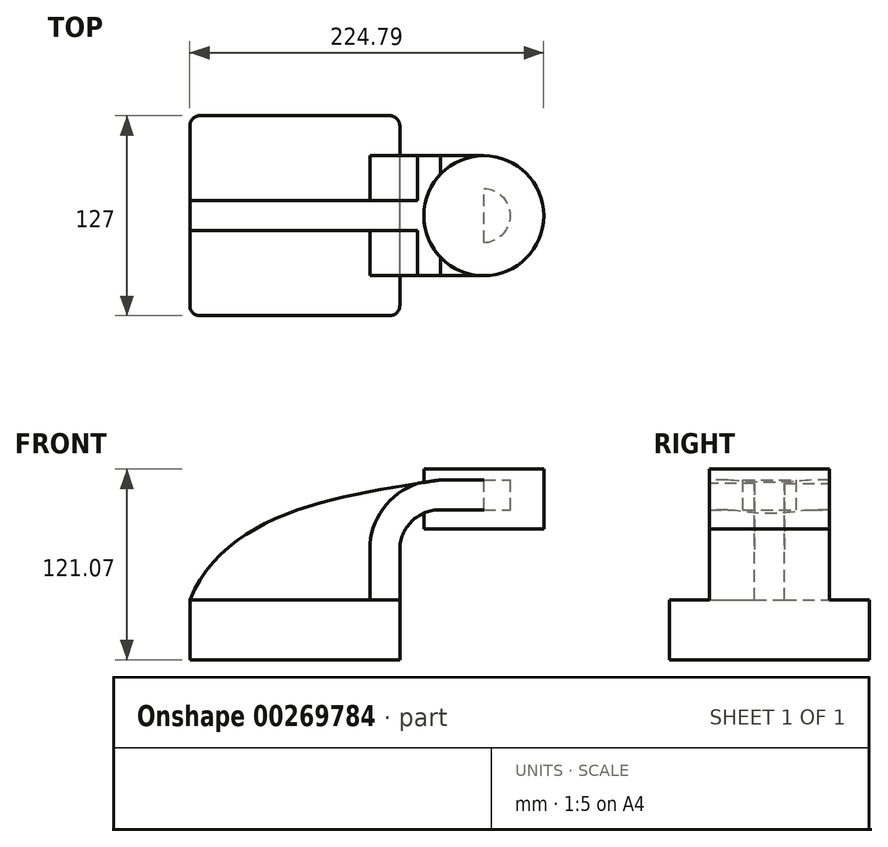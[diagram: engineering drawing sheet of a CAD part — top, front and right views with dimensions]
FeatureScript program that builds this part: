
annotation { "Feature Type Name" : "Feature", "Feature Type Description" : "" }
export const myFeature = defineFeature(function(context is Context, id is Id, definition is map)
    precondition{}
    {
        {
            var Q0;
            Q0=qCreatedBy(makeId("Front.planeOp"),FACE);
            var sketch = newSketch(context, id + "F0", { "sketchPlane" : qUnion([Q0])});
            skLineSegment(sketch, "E0.bottom", {"start": v(-66.68, 19.05) * mm, "end": v(66.67, 19.05) * mm});
            skLineSegment(sketch, "E0.top", {"start": v(-66.68, -19.05) * mm, "end": v(66.68, -19.05) * mm});
            skLineSegment(sketch, "E0.left", {"start": v(-66.68, 19.05) * mm, "end": v(-66.67, -19.05) * mm});
            skLineSegment(sketch, "E0.right", {"start": v(66.68, 19.05) * mm, "end": v(66.68, -19.05) * mm});
            skPoint(sketch, "E0.middle", {"position": v(0, 0) * mm});
            skLineSegment(sketch, "E1.bottom", {"start": v(120.01, 102.02) * mm, "end": v(158.11, 102.02) * mm});
            skLineSegment(sketch, "E1.top", {"start": v(120.01, 63.92) * mm, "end": v(158.11, 63.92) * mm});
            skLineSegment(sketch, "E1.left", {"start": v(120.01, 102.02) * mm, "end": v(120.01, 63.92) * mm});
            skLineSegment(sketch, "E1.right", {"start": v(158.11, 102.02) * mm, "end": v(158.11, 63.92) * mm});
            skPoint(sketch, "E1.middle", {"position": v(139.06, 82.97) * mm});
            skLineSegment(sketch, "E2", {"start": v(66.67, 19.05) * mm, "end": v(66.67, 50.8) * mm});
            skArc(sketch, "E3", {"start": v(66.67, 50.8) * mm, "mid": v(74.27, 68.91) * mm, "end": v(92.51, 76.2) * mm});
            skLineSegment(sketch, "E4", {"start": v(92.51, 76.2) * mm, "end": v(136.96, 76.2) * mm});
            skLineSegment(sketch, "E5.0", {"start": v(92.65, 95.25) * mm, "end": v(136.96, 95.25) * mm});
            skArc(sketch, "E5.1", {"start": v(47.62, 50.8) * mm, "mid": v(60.85, 82.43) * mm, "end": v(92.65, 95.25) * mm});
            skLineSegment(sketch, "E5.2", {"start": v(47.62, 19.05) * mm, "end": v(47.62, 50.8) * mm});
            skLineSegment(sketch, "E6", {"start": v(136.96, 95.25) * mm, "end": v(136.96, 76.2) * mm});
            skFitSpline(sketch, "E7", {"points": [v(-66.68, 19.05) * mm, v(92.65, 95.25) * mm], "startDerivative": vector(70, 169.2) * mm, "endDerivative": vector(193.9, 30.04) * mm});
            skSolve(sketch);
        }
        {
            var Q0;
            Q0=makeQuery(id+"F0.imprint","IMPRINT",FACE,{"disambiguationData":[TD([[makeQuery(id+"F0.imprint","IMPRINT",EDGE,{"derivedFrom":sQuery(id+"F0.wireOp",EDGE,"E0.top")}),1.0]])]});
            extrude(context, id + "F1", {"entities" : qUnion([Q0]), "endBound" : BoundingType.SYMMETRIC, "depth" : 127 * mm});
        }
        {
            var Q0;
            {var subQ3=sQuery(id+"F0.wireOp",EDGE,"E5.2");Q0=makeQuery(id+"F0.imprint","IMPRINT",FACE,{"disambiguationData":[TD([[makeQuery(id+"F0.imprint","IMPRINT",EDGE,{"derivedFrom":subQ3}),1.0]])]});}
            extrude(context, id + "F2", {"entities" : qUnion([Q0]), "operationType" : NewBodyOperationType.ADD, "endBound" : BoundingType.SYMMETRIC, "depth" : 19.05 * mm});
        }
        {
            var Q0;
            {var subQ1=sQuery(id+"F0.wireOp",EDGE,"E2");Q0=makeQuery(id+"F0.imprint","IMPRINT",FACE,{"disambiguationData":[TD([[makeQuery(id+"F0.imprint","IMPRINT",EDGE,{"derivedFrom":subQ1}),1.0]])]});}
            extrude(context, id + "F3", {"entities" : qUnion([Q0]), "operationType" : NewBodyOperationType.ADD, "endBound" : BoundingType.SYMMETRIC, "depth" : 76.2 * mm});
        }
        {
            var Q0;
            {var subQ4=sQuery(id+"F0.wireOp",EDGE,"E1.bottom");Q0=makeQuery(id+"F0.imprint","IMPRINT",FACE,{"disambiguationData":[TD([[makeQuery(id+"F0.imprint","IMPRINT",EDGE,{"derivedFrom":subQ4}),-1.0]])]});}
            var Q1;
            Q1=sQuery(id+"F0.wireOp",EDGE,"E1.left");
            revolve(context, id + "F4", {"operationType" : NewBodyOperationType.ADD, "entities" : qUnion([Q0]), "axis" : qUnion([Q1]), "revolveType" : RevolveType.FULL});
        }
        {
            var Q0;
            Q0=makeQuery(id+"F1.opExtrude","CAP_EDGE",EDGE,{"disambiguationData":[OSD([sQuery(id+"F0.wireOp",EDGE,"E0.left")])],"isStart":false});
            var Q1;
            Q1=makeQuery(id+"F1.opExtrude","CAP_EDGE",EDGE,{"disambiguationData":[OSD([sQuery(id+"F0.wireOp",EDGE,"E0.right")])],"isStart":false});
            var Q2;
            Q2=makeQuery(id+"F1.opExtrude","CAP_EDGE",EDGE,{"disambiguationData":[OSD([sQuery(id+"F0.wireOp",EDGE,"E0.right")])],"isStart":true});
            var Q3;
            Q3=makeQuery(id+"F1.opExtrude","CAP_EDGE",EDGE,{"disambiguationData":[OSD([sQuery(id+"F0.wireOp",EDGE,"E0.left")])],"isStart":true});
            fillet(context, id + "F5", {"entities" : qUnion([Q0, Q1, Q2, Q3]), "radius" : 6.35 * mm, "tangentPropagation" : true, "allowEdgeOverflow" : false});
        }
    });
